# Revit family: SW260
name_source: partatom
category: Plumbing Fixtures
units: mm (PartAtom-declared; Revit-internal decimal feet)

## family parameters
Cut with Voids When Loaded = No
Host = Face
Maintain Annotation Orientation = No
OmniClass Number = 23.45.05.14.14
OmniClass Title = Sinks/Lavatories
Part Type = Normal
Room Calculation Point = No
Round Connector Dimension = Use Diameter
Shared = Yes

## types (1)
- SW260
    Assembly Code = D2010310
    CW Connection = No
    CWFU = 1.5
    Deck Height = 34"
    Default Elevation = 0"
    Description = One-Station Wash-Ware Eco-Trough Stainless Steel Trough Sink
    EG10 Enviro-Glaze Color (White) = No
    Faucet Hole Distance = 4"
    Finish = Stainless_Steel-Acorn-Satin
    Flow Rate = 0.5 GPM (1.9 LPM)
    HW Connection = No
    HWFU = 1.5
    Height = 6 1/2"
    IAPMO Compliance = Uniform Plumbing Code (UPC ), ® National Plumbing Code of Canada (cUPC ) and ASME A112.19.3.
    Installation Instruction Link = https://www.acorneng.com
    Installation Type = Wall Mounted
    Length = 16"
    Manufacturer = Acorn Engineering
    Material = Stainless_Steel-Acorn-Satin
    Model = SW260-34
    Optional 1-1/2” Tail piece & P-trap = Yes
    Product Documentation Link = https://www.acorneng.com
    Product Page URL = https://www.acorneng.com
    SW000-24   Front Support Legs, 24” Rim Height (Child) = No
    SW000-30   Front Support Legs, 30” Rim Height (Junior) = No
    SW000-34 Front Support Legs, 34” Rim Height (Adult) = No
    SW000-F50 H&C Wristblade Faucet, Gooseneck Spout = No
    SW000-F51 H&C Wristblade Faucet, Spout = No
    SW000-F60 S/T Sensor Operated Faucet, J Spout, Plate = No
    SW000-F70 S/T Pushbutton Metering Faucet, Plate = No
    SW000-PT   Daisy Strainer, Tailpiece, 1-1/2” P-Trap, Plastic = No
    SW000-PTC Daisy Strainer, Tailpiece, 1-1/2” P-Trap, Chrome = No
    SW000-SG   Splash Guard, (Multi-Station Units) = No
    URL = http://www.acorneng.com
    Vent Connection = No
    WFU = 2
    WH-DECAL  10” Sticky Decal “Wash Your Hands” = No
    Waste Connection = Yes
    Waste Connection Diameter = 1 1/2"
    Width = 60"

## geometry (parser evidence)
native form markers: Sweep x2
no freeform markers — native parametric forms only
